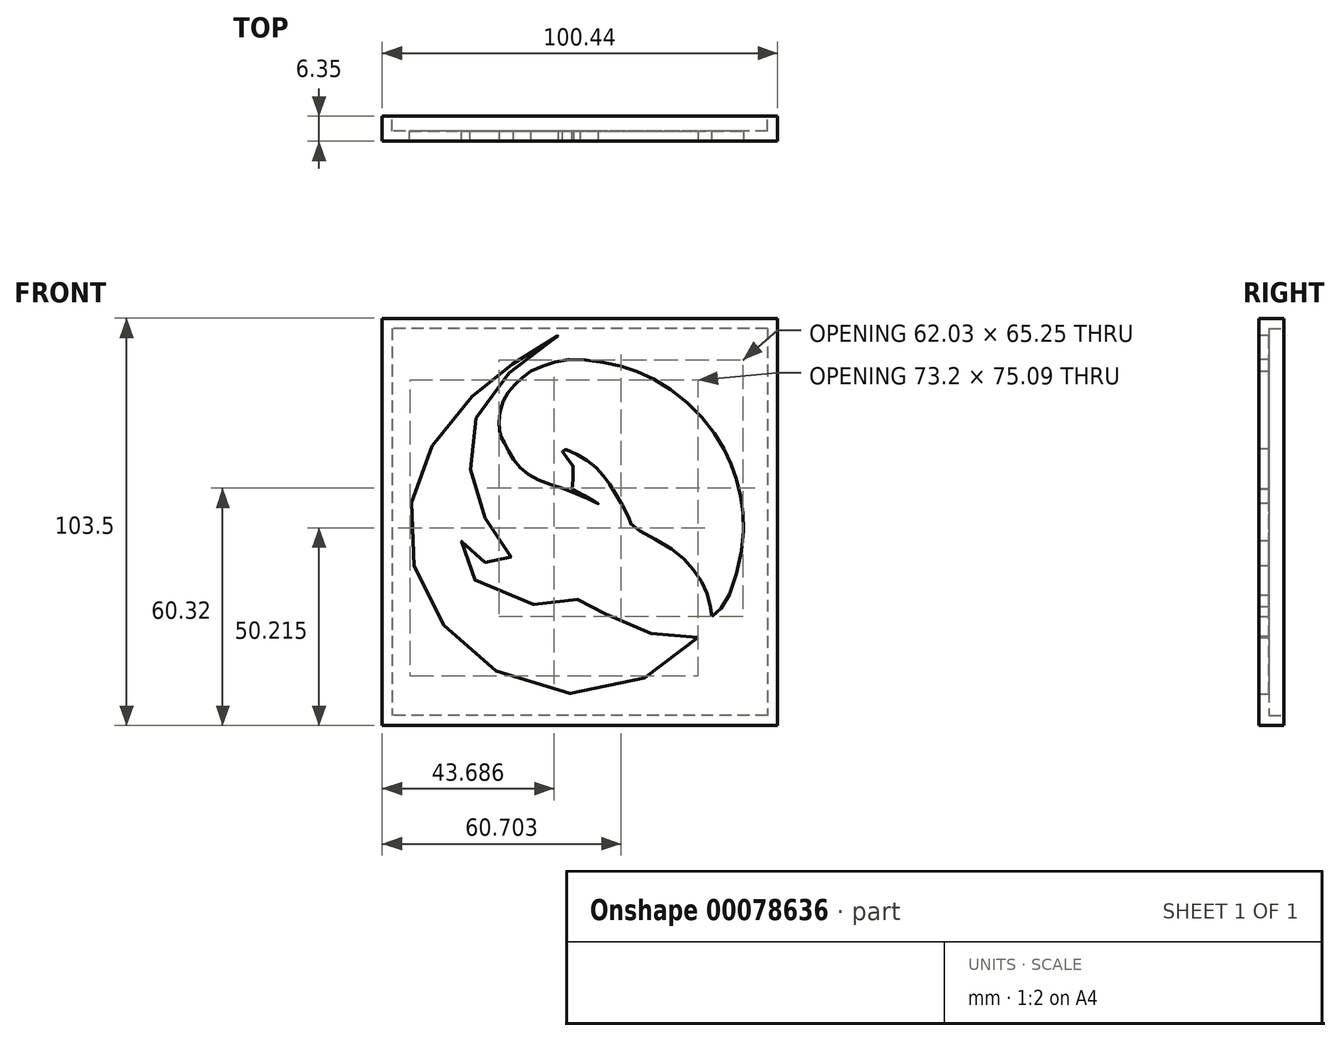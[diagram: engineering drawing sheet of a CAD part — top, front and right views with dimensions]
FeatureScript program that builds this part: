
annotation { "Feature Type Name" : "Feature", "Feature Type Description" : "" }
export const myFeature = defineFeature(function(context is Context, id is Id, definition is map)
    precondition{}
    {
        {
            var Q0;
            Q0=qCreatedBy(makeId("Front.planeOp"),FACE);
            var sketch = newSketch(context, id + "F0", { "sketchPlane" : qUnion([Q0])});
            skPoint(sketch, "E0", {"position": v(0, 0) * mm});
            skFitSpline(sketch, "E1", {"points": [v(-12.42, 38.39) * mm, v(-7.7, 40.2) * mm, v(-1.7, 41.3) * mm, v(7.82, 40.2) * mm, v(16.64, 37.28) * mm, v(26.96, 30.6) * mm, v(35.3, 20.75) * mm, v(39.08, 12.95) * mm, v(41.16, 4.34) * mm, v(41.25, -5.73) * mm, v(37.23, -19.97) * mm, v(33.52, -24.05) * mm], "startDerivative": vector(68.51, 28.4) * mm, "endDerivative": vector(-54.4, -43.11) * mm});
            skFitSpline(sketch, "E2", {"points": [v(33.52, -24.05) * mm, v(32.44, -18.59) * mm, v(29.13, -12.4) * mm, v(22.27, -6.2) * mm, v(13.2, -0.78) * mm, v(12.38, 1.2) * mm, v(8.81, 7.54) * mm, v(6.66, 10.87) * mm, v(3.28, 14.55) * mm, v(-1.08, 17.35) * mm, v(-4.5, 18.38) * mm, v(-3.2, 16.11) * mm, v(-1.59, 13.7) * mm, v(-1.98, 8.43) * mm, v(-1.98, 8.43) * mm], "startDerivative": vector(-9.2, 69.66) * mm, "endDerivative": vector(-27.8, -14.74) * mm});
            skFitSpline(sketch, "E3", {"points": [v(-1.98, 8.43) * mm, v(4.65, 4.64) * mm, v(-1.98, 7.63) * mm, v(-14.2, 12.81) * mm, v(-19.02, 19.7) * mm, v(-20.5, 23.5) * mm, v(-18.9, 31.78) * mm, v(-12.42, 38.39) * mm], "startDerivative": vector(72.68, -39.25) * mm, "endDerivative": vector(49.39, 37.63) * mm});
            skFitSpline(sketch, "E4", {"points": [v(30.07, -29.3) * mm, v(22.77, -29.3) * mm, v(16.96, -27.8) * mm, v(10.38, -25.23) * mm, v(2.11, -20.77) * mm, v(-1.44, -18.58) * mm, v(0, -20.45) * mm, v(0, -21.03) * mm, v(-13.38, -20.7) * mm, v(-25.26, -15.9) * mm, v(-29.08, -11.34) * mm, v(-29.98, -5.57) * mm, v(-29.98, -4.67) * mm, v(-28.76, -6.95) * mm, v(-24.85, -9.96) * mm, v(-18.26, -11.02) * mm, v(-16.8, -10.04) * mm, v(-18.1, -8.25) * mm, v(-21.35, -4.02) * mm, v(-25.75, 4.6) * mm, v(-27.66, 11.02) * mm, v(-27.56, 20.1) * mm, v(-26.08, 27.02) * mm, v(-20.5, 34.9) * mm, v(-12.76, 42.55) * mm, v(-5.41, 47.48) * mm, v(-12.86, 43.52) * mm, v(-22.82, 35) * mm, v(-27.37, 31.9) * mm, v(-35.1, 23.4) * mm, v(-41, 11.3) * mm, v(-43.04, 2.6) * mm, v(-42.27, -10.33) * mm, v(-36.85, -22.98) * mm, v(-28.07, -32.92) * mm, v(-14.26, -41.31) * mm, v(4.33, -43.38) * mm, v(21.25, -36.93) * mm, v(30.07, -29.3) * mm]});
            skSolve(sketch);
        }
        {
            var Q0;
            Q0=qCreatedBy(makeId("Front.planeOp"),FACE);
            var sketch = newSketch(context, id + "F1", { "sketchPlane" : qUnion([Q0])});
            skLineSegment(sketch, "E5.bottom", {"start": v(50.22, 51.75) * mm, "end": v(-50.22, 51.75) * mm});
            skLineSegment(sketch, "E5.top", {"start": v(50.22, -51.75) * mm, "end": v(-50.22, -51.75) * mm});
            skLineSegment(sketch, "E5.left", {"start": v(50.22, 51.75) * mm, "end": v(50.22, -51.75) * mm});
            skLineSegment(sketch, "E5.right", {"start": v(-50.22, 51.75) * mm, "end": v(-50.22, -51.75) * mm});
            skPoint(sketch, "E5.middle", {"position": v(0, 0) * mm});
            skSolve(sketch);
        }
        {
            var Q0;
            Q0=qSketchRegion(id+"F1",true);
            extrude(context, id + "F2", {"entities" : qUnion([Q0]), "depth" : 6.35 * mm});
        }
        {
            var Q0;
            Q0=makeQuery(id+"F2.opExtrude","CAP_FACE",FACE,{"disambiguationData":[OSD([sQuery(id+"F1.wireOp",EDGE,"E5.bottom"),sQuery(id+"F1.wireOp",EDGE,"E5.top"),sQuery(id+"F1.wireOp",EDGE,"E5.left"),sQuery(id+"F1.wireOp",EDGE,"E5.right")])],"isStart":true});
            shell(context, id + "F3", {"entities" : qUnion([Q0]), "thickness" : 2.54 * mm});
        }
        {
            var Q0;
            Q0=qSketchRegion(id+"F0",true);
            extrude(context, id + "F4", {"entities" : qUnion([Q0]), "operationType" : NewBodyOperationType.REMOVE, "endBound" : BoundingType.THROUGH_ALL, "depth" : 25.4 * mm});
        }
    });
